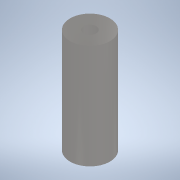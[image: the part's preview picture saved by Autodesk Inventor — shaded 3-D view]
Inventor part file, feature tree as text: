
AUTODESK INVENTOR PART (.ipt)
format: ipt  version: 2022 (Build 260153000, 153)  size: 95,744 bytes
history: native  units: in
note: dims shown in document units (in); Inventor stores cm internally (conversion verified against a paired STEP export)
features: extrude x1, sketch x1
ambient origin geometry x8: Origin, YZ Plane, XZ Plane, XY Plane, X Axis, Y Axis, Z Axis, Center Point
bodies: Solid1 (feature_tree)
feature tree (2):
  extrude  "Extrusion1"  Depth=1.6535in
  sketch  "Sketch1"  dims[d0=0.1969in d1=0.6299in d2=1.6535in d3=0.0in]
